# Revit family: 72687257 - iCON30 - BIM file
name_source: partatom
category: Mechanical Equipment
units: mm (PartAtom-declared; Revit-internal decimal feet)

## family parameters
Cut with Voids When Loaded = No
Host = Face
Maintain Annotation Orientation = No
Part Type = Normal
Room Calculation Point = No
Round Connector Dimension = Use Diameter
Shared = No

## types (1)
- iC30
    2SFT = iCON30_Modules : 2 Speed Humidity Pull Cord Boost
    6MonthlyMaintenance = Visually inspect system, clean the fan and ducting if necessary
    A = 225 mm  [stored 0.738189 ft]
    AccessClearanceBottom = 350 mm
    AccessClearanceFront = 350 mm
    AccessClearanceLeft = 350 mm
    AccessClearanceRear = 0 mm  [stored 0 ft]
    AccessClearanceRight = 350 mm
    AccessClearanceTop = 350 mm
    AnthraciteFT = CADS_AIRFLOWdev_Fan_iCON30_Covers : iCON_Cover_Anthracite
    AssemblyPlace = UKNOWN
    AssetType = Fixed
    BMSLinks = No
    Body = CADS_AirFlow_White
    CEApproval = Yes
    Category = Pr_65_67_29_52:Mixed Flow Fans
    Color = White
(optional Anthracite (52634506), Sandstone (52634508) and Silver (52634507) covers are available)
    Controls = Basic on/off functionality controlled by external switch
The following additional, interchangeable modules can be fitted to the iCON30:
Pull cord (72573602)
Timer (72612601)
Humidity, Pull cord with Timer (72687103)
Motion sensor with timer overrun (72687104)
Motion sensor humidity timer (72687102)
Continuous Ventilation at 8/13 l/sec (72675701)
Delayed Timer with Pull cord (72675702)
2 Speed Humidity Pull Cord Boost (72675703)
    D = 97 mm  [stored 0.318241 ft]
    DTFT = iCON30_Modules : Delayed Timer With Pull Cord
    Default Elevation = 1219 mm
    Description = An intermittent extract fan with interchangeable modular controls and covers and a Red Dot Design Award winner
    DesignOfDomesticVentilation = This fan should provide the minimum flow rates outlined and installed in line with Approved Document Part F of the Building Regulations.
    Ductwork = 100mm flexible or rigid
    DurationUnit = Year
    E = 43 mm  [stored 0.141076 ft]
    ErPEnergyRating = D
    Exclusions = Hasn't been installed or used in accordance with the instructions
Connected with an unsuitable electrical supply
Has been misused, neglected or damaged
Modified or repaired by someone not authorised by Airflow Developments Ltd
Hasn't been installed according to Building Regulations or IEEE wiring regulations
    ExpectedServiceLife = 3
    Export Type to IFC As = IfcFanType
    ExternalExhaustAirTerminals = 90% free air grille
    F = 51 mm
    Fan = Domestic intermittent mixed flow fan
    Features = Up to 33l/sec
Stylish design, with unique iris shutter
Interchangeable modular control
IPX4 rated
Sound Levels from only 30.3dB(A)
Red Dot Design Award Winner
Choice of recessed or surface mounted with skirt supplied
    Finish = Matte
    FireControlPanelLinks = No
    G = 20 mm  [stored 0.0656168 ft]
    GlobalTradeItemNumber = 5019009331195
    Grade = Virgin
    GrossWeight = 1.11 kg
    H = 30 mm  [stored 0.0984252 ft]
    HPCFT = iCON30_Modules : Humidity Pull Cord With Timer Overrun
    HasPartWinding = Yes
    HasProtectiveEarth = No
    I = 148 mm  [stored 0.485564 ft]
    IP_Code = IPX4
    ISO140001 = Yes
    ISO90001 = Yes
    IfcExportAs = IfcFanType
    IfcExportType = NOTDEFINED
    InsulationStandardClass = Double Insulated
    IsExtendedWarranty = No
    IsGuarded = Yes
    MSHFT = iCON30_Modules : Motion Sensor Humidity Timer
    MSTFT = iCON30_Modules : Motion Sensor With Timer Overrun
    Manufacturer = Airflow Developments Ltd
    ManufacturerAddress = Aidelle House
Lancaster Road
Cressex Business Park
High Wycombe
Bucks
HP123QP
    ManufacturerTelephone = 01494 525252
    ManufacturerWebsite = www.airflow.com
    Material = Plastic
    Maximum air flow = 121 m3/h
    ModelLabel = iCON 30
    ModelReference = 72687257
    MotorDriveType = Direct Drive
    MotorEnclosureType = Totally Enclosed Air Over
    NBSCode = 90-45-30/340 Mixed flow fans;
    NominalAirFlowRate = 33.0 L/s
    NominalFrequencyRange = 50-60
    NominalHeight = 225 mm  [stored 0.738189 ft]
    NominalLength = 225 mm  [stored 0.738189 ft]
    NominalPowerRate = 11 W
    NominalRotationSpeed = 50 Hz
    NominalStaticPressure = 90.0 Pa
    NominalWidth = 144 mm
    NumberOfPoles = 1
    OperationTemperatureRange = up to 40°C
    PCFT = iCON30_Modules : Pull Cord
    PointOfContact = Airflow Developments Ltd
    PowerSource = System-powered
    ProductionYear = 2017
    Quantity = 1
    QuietMarkApproval = No
    RatedCurrent = 3 A
    RatedVoltage = 230 V
    RedDotDesignAward = Yes
    ReplacementCost = 145.572
    RoomExtractAirTerminalDevices = Utility room and kitchen fan (adjacent to the hob) fan
    SandstoneFT = CADS_AIRFLOWdev_Fan_iCON30_Covers : iCON_Cover_Sandstone
    ServiceLifeDuration = 3
    ServiceLifeType = ExpectedServiceLife
    Shape = Round
    ShippingWeight = 1.60 kg
    SilverFT = CADS_AIRFLOWdev_Fan_iCON30_Covers : iCON_Cover_Silver
    Size = 144 x 225 x 225
    StartingTime = 5.0 s
    Status = New
    SupplyPhase = 1
    Type = iC30
    Type IFC Predefined Type = NOTDEFINED
    Uniclass2015 = Pr_65_67_29_52
    WarrantyContent = Covered against faulty material or workmanship - not reinstallation if needed
    WarrantyGuarantor = Airflow Developments Ltd
    WarrantyPeriod = 2
    WarrantyPeriodForMotors = 1
    WarrantyPeriodWhenRegistered = 3

note: [stored X ft] marks values corroborated as IEEE doubles in the binary element streams (Revit-internal decimal feet)

## geometry (parser evidence)
native form markers: Blend x10, Sweep x9
no freeform markers — native parametric forms only
